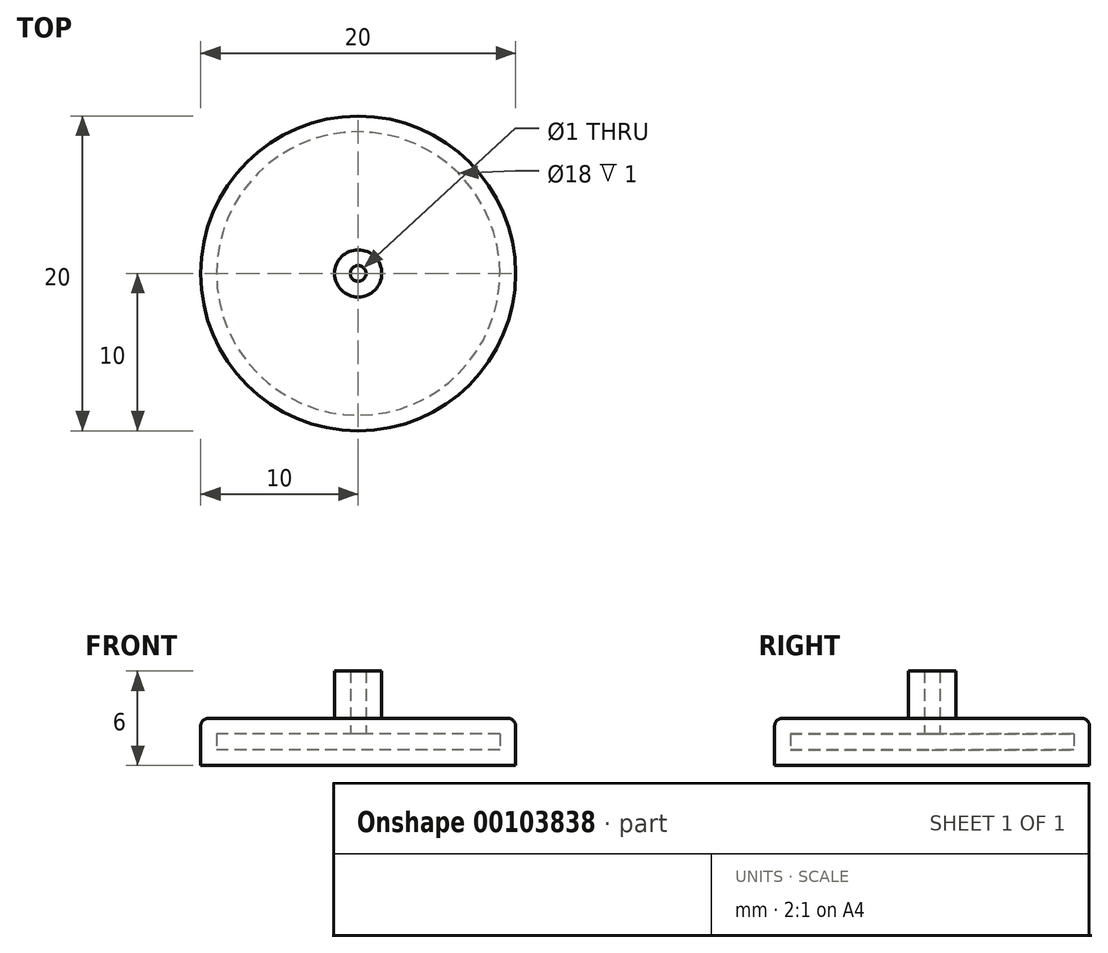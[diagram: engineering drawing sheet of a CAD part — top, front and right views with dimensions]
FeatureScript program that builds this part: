
annotation { "Feature Type Name" : "Feature", "Feature Type Description" : "" }
export const myFeature = defineFeature(function(context is Context, id is Id, definition is map)
    precondition{}
    {
        {
            var Q0;
            Q0=qCreatedBy(makeId("Top.planeOp"),FACE);
            var sketch = newSketch(context, id + "F0", { "sketchPlane" : qUnion([Q0])});
            skCircle(sketch, "E0", {"center": v(0, 0) * mm, "radius": 10 * mm});
            skSolve(sketch);
        }
        {
            var Q0;
            Q0=makeQuery(id+"F0.imprint","IMPRINT",FACE,{"disambiguationData":[TD([[makeQuery(id+"F0.imprint","IMPRINT",EDGE,{"derivedFrom":sQuery(id+"F0.wireOp",EDGE,"E0")}),1.0]])]});
            extrude(context, id + "F1", {"entities" : qUnion([Q0]), "depth" : 1 * mm});
        }
        {
            var Q0;
            Q0=makeQuery(id+"F1.opExtrude","CAP_FACE",FACE,{"disambiguationData":[OSD([sQuery(id+"F0.wireOp",EDGE,"E0")])],"isStart":false});
            var sketch = newSketch(context, id + "F2", { "sketchPlane" : qUnion([Q0])});
            skCircle(sketch, "E1", {"center": v(0, 0) * mm, "radius": 10 * mm});
            skCircle(sketch, "E2", {"center": v(0, 0) * mm, "radius": 9 * mm});
            skSolve(sketch);
        }
        {
            var Q0;
            Q0=makeQuery(id+"F2.imprint","IMPRINT",FACE,{"disambiguationData":[TD([[makeQuery(id+"F2.imprint","IMPRINT",EDGE,{"derivedFrom":sQuery(id+"F2.wireOp",EDGE,"E1")}),1.0]])]});
            extrude(context, id + "F3", {"entities" : qUnion([Q0]), "operationType" : NewBodyOperationType.ADD, "depth" : 1 * mm});
        }
        {
            var Q0;
            Q0=makeQuery(id+"F3.opExtrude","CAP_FACE",FACE,{"disambiguationData":[OSD([sQuery(id+"F2.wireOp",EDGE,"E1"),sQuery(id+"F2.wireOp",EDGE,"E2")])],"isStart":false});
            var sketch = newSketch(context, id + "F4", { "sketchPlane" : qUnion([Q0])});
            skCircle(sketch, "E3", {"center": v(0, 0) * mm, "radius": 10 * mm});
            skCircle(sketch, "E4", {"center": v(0, 0) * mm, "radius": 0.5 * mm});
            skSolve(sketch);
        }
        {
            var Q0;
            Q0 = qSketchRegion(id + "F4", true);
            extrude(context, id + "F5", {"entities" : qUnion([Q0]), "operationType" : NewBodyOperationType.ADD, "depth" : 1 * mm});
        }
        {
            var Q0;
            Q0=makeQuery(id+"F5.opExtrude","CAP_FACE",FACE,{"disambiguationData":[OSD([sQuery(id+"F4.wireOp",EDGE,"E3"),sQuery(id+"F4.wireOp",EDGE,"E4")])],"isStart":false});
            var sketch = newSketch(context, id + "F6", { "sketchPlane" : qUnion([Q0])});
            skCircle(sketch, "E5", {"center": v(0, 0) * mm, "radius": 0.5 * mm});
            skCircle(sketch, "E6", {"center": v(0, 0) * mm, "radius": 1.5 * mm});
            skSolve(sketch);
        }
        {
            var Q0;
            Q0 = qSketchRegion(id + "F6", true);
            extrude(context, id + "F7", {"entities" : qUnion([Q0]), "operationType" : NewBodyOperationType.ADD, "depth" : 3 * mm});
        }
        {
            var Q0;
            Q0=makeQuery(id+"F5.opExtrude","CAP_EDGE",EDGE,{"disambiguationData":[OSD([sQuery(id+"F4.wireOp",EDGE,"E3")])],"isStart":false});
            fillet(context, id + "F8", {"entities" : qUnion([Q0]), "radius" : 0.5 * mm, "tangentPropagation" : true, "allowEdgeOverflow" : false});
        }
    });
